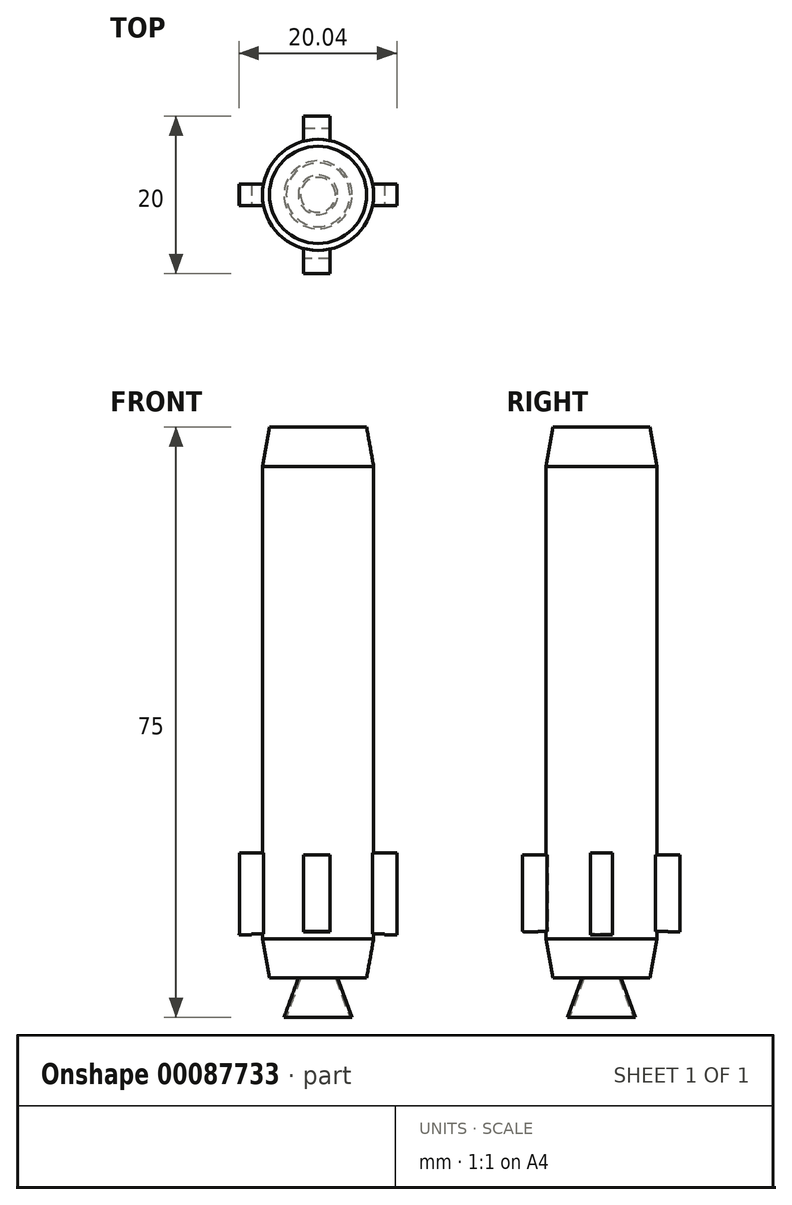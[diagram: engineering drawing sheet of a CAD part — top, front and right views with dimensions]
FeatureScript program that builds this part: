
annotation { "Feature Type Name" : "Feature", "Feature Type Description" : "" }
export const myFeature = defineFeature(function(context is Context, id is Id, definition is map)
    precondition{}
    {
        {
            var Q0;
            Q0=qCreatedBy(makeId("Top.planeOp"),FACE);
            var sketch = newSketch(context, id + "F0", { "sketchPlane" : qUnion([Q0])});
            skCircle(sketch, "E0", {"center": v(0, 0) * mm, "radius": 7.06 * mm});
            skSolve(sketch);
        }
        {
            var Q0;
            Q0 = qSketchRegion(id + "F0", true);
            extrude(context, id + "F1", {"entities" : qUnion([Q0]), "depth" : 10 * mm, "hasSecondDirection" : true, "secondDirectionOppositeDirection" : true, "secondDirectionDepth" : 50 * mm});
        }
        {
            var Q0;
            Q0=makeQuery(id+"F1.opExtrude","CAP_FACE",FACE,{"disambiguationData":[OSD([sQuery(id+"F0.wireOp",EDGE,"E0")])],"isStart":false});
            extrude(context, id + "F2", {"entities" : qUnion([Q0]), "operationType" : NewBodyOperationType.ADD, "depth" : 5 * mm, "hasDraft" : true, "draftAngle" : 10 * degree, "draftPullDirection" : true});
        }
        {
            var Q0;
            Q0=makeQuery(id+"F1.opExtrude","CAP_FACE",FACE,{"disambiguationData":[OSD([sQuery(id+"F0.wireOp",EDGE,"E0")])],"isStart":true});
            extrude(context, id + "F3", {"entities" : qUnion([Q0]), "operationType" : NewBodyOperationType.ADD, "depth" : 5 * mm, "hasDraft" : true, "draftAngle" : 10 * degree, "draftPullDirection" : true});
        }
        {
            var Q0;
            Q0=makeQuery(id+"F3.opExtrude","CAP_FACE",FACE,{"disambiguationData":[OSD([sQuery(id+"F0.wireOp",EDGE,"E0")])],"isStart":false});
            var sketch = newSketch(context, id + "F4", { "sketchPlane" : qUnion([Q0])});
            skCircle(sketch, "E1", {"center": v(0, 0) * mm, "radius": 2.5 * mm});
            skSolve(sketch);
        }
        {
            var Q0;
            Q0 = qSketchRegion(id + "F4", true);
            extrude(context, id + "F5", {"entities" : qUnion([Q0]), "operationType" : NewBodyOperationType.ADD, "depth" : 5 * mm, "hasDraft" : true, "draftAngle" : 20 * degree});
        }
        {
            var Q0;
            Q0=makeQuery(id+"F5.opExtrude","CAP_FACE",FACE,{"disambiguationData":[OSD([sQuery(id+"F4.wireOp",EDGE,"E1")])],"isStart":false});
            var sketch = newSketch(context, id + "F6", { "sketchPlane" : qUnion([Q0])});
            skCircle(sketch, "E2", {"center": v(0, 0) * mm, "radius": 4.04 * mm});
            skSolve(sketch);
        }
        {
            var Q0;
            Q0 = qSketchRegion(id + "F6", true);
            extrude(context, id + "F7", {"entities" : qUnion([Q0]), "operationType" : NewBodyOperationType.REMOVE, "oppositeDirection" : true, "depth" : 5 * mm, "hasDraft" : true, "draftAngle" : 20 * degree, "draftPullDirection" : true});
        }
        {
            var Q0;
            Q0=qCreatedBy(makeId("Right.planeOp"),FACE);
            var sketch = newSketch(context, id + "F8", { "sketchPlane" : qUnion([Q0])});
            skLineSegment(sketch, "E3.bottom", {"start": v(-1.38, -49.39) * mm, "end": v(1.38, -49.39) * mm});
            skLineSegment(sketch, "E3.top", {"start": v(-1.38, -39.07) * mm, "end": v(1.38, -39.07) * mm});
            skLineSegment(sketch, "E3.left", {"start": v(-1.38, -49.39) * mm, "end": v(-1.38, -39.07) * mm});
            skLineSegment(sketch, "E3.right", {"start": v(1.38, -49.39) * mm, "end": v(1.38, -39.07) * mm});
            skSolve(sketch);
        }
        {
            var Q0;
            Q0 = qSketchRegion(id + "F8", true);
            extrude(context, id + "F9", {"entities" : qUnion([Q0]), "operationType" : NewBodyOperationType.ADD, "depth" : 10 * mm, "hasSecondDirection" : true, "secondDirectionOppositeDirection" : true, "secondDirectionDepth" : 10 * mm});
        }
        {
            var Q0;
            {var subQ0=sQuery(id+"F8.wireOp",EDGE,"E3.left");var subQ1=sQuery(id+"F8.wireOp",EDGE,"E3.right");var subQ2=sQuery(id+"F8.wireOp",EDGE,"E3.bottom");Q0=makeQuery(id+"F9.boolean.opBoolean","SPLIT",FACE,{"disambiguationData":[TD([makeQuery(id+"F9.opExtrude","CAP_FACE",FACE,{"disambiguationData":[OSD([subQ2,sQuery(id+"F8.wireOp",EDGE,"E3.top"),subQ0,subQ1])],"isStart":false})])],"derivedFrom":makeQuery(id+"F9.opExtrude","SWEPT_FACE",FACE,{"disambiguationData":[OSD([subQ2])]})});}
            var sketch = newSketch(context, id + "F10", { "sketchPlane" : qUnion([Q0])});
            skLineSegment(sketch, "E4.bottom", {"start": v(10, -1.38) * mm, "end": v(8.46, -1.38) * mm});
            skLineSegment(sketch, "E4.top", {"start": v(10, 1.38) * mm, "end": v(8.46, 1.38) * mm});
            skLineSegment(sketch, "E4.left", {"start": v(10, -1.38) * mm, "end": v(10, 1.38) * mm});
            skLineSegment(sketch, "E4.right", {"start": v(8.46, -1.38) * mm, "end": v(8.46, 1.38) * mm});
            skLineSegment(sketch, "E5.bottom", {"start": v(-10.04, -1.38) * mm, "end": v(-8.44, -1.38) * mm});
            skLineSegment(sketch, "E5.top", {"start": v(-10.04, 1.38) * mm, "end": v(-8.44, 1.38) * mm});
            skLineSegment(sketch, "E5.left", {"start": v(-10.04, -1.38) * mm, "end": v(-10.04, 1.38) * mm});
            skLineSegment(sketch, "E5.right", {"start": v(-8.44, -1.38) * mm, "end": v(-8.44, 1.38) * mm});
            skSolve(sketch);
        }
        {
            var Q0;
            Q0 = qSketchRegion(id + "F10", true);
            extrude(context, id + "F11", {"entities" : qUnion([Q0]), "operationType" : NewBodyOperationType.ADD, "depth" : 0.1 * mm});
        }
        {
            var Q0;
            Q0=qCreatedBy(makeId("Front.planeOp"),FACE);
            var sketch = newSketch(context, id + "F12", { "sketchPlane" : qUnion([Q0])});
            skLineSegment(sketch, "E6.bottom", {"start": v(1.53, -39.38) * mm, "end": v(-1.86, -39.38) * mm});
            skLineSegment(sketch, "E6.top", {"start": v(1.53, -49.07) * mm, "end": v(-1.86, -49.07) * mm});
            skLineSegment(sketch, "E6.left", {"start": v(1.53, -39.38) * mm, "end": v(1.53, -49.07) * mm});
            skLineSegment(sketch, "E6.right", {"start": v(-1.86, -39.38) * mm, "end": v(-1.86, -49.07) * mm});
            skSolve(sketch);
        }
        {
            var Q0;
            Q0 = qSketchRegion(id + "F12", true);
            extrude(context, id + "F13", {"entities" : qUnion([Q0]), "operationType" : NewBodyOperationType.ADD, "depth" : 10 * mm, "hasSecondDirection" : true, "secondDirectionOppositeDirection" : true, "secondDirectionDepth" : 10 * mm});
        }
        {
            var Q0;
            {var subQ0=sQuery(id+"F12.wireOp",EDGE,"E6.right");var subQ1=sQuery(id+"F12.wireOp",EDGE,"E6.left");var subQ2=sQuery(id+"F12.wireOp",EDGE,"E6.top");Q0=makeQuery(id+"F13.boolean.opBoolean","SPLIT",FACE,{"disambiguationData":[TD([makeQuery(id+"F13.opExtrude","CAP_FACE",FACE,{"disambiguationData":[OSD([sQuery(id+"F12.wireOp",EDGE,"E6.bottom"),subQ2,subQ1,subQ0])],"isStart":true})])],"derivedFrom":makeQuery(id+"F13.opExtrude","SWEPT_FACE",FACE,{"disambiguationData":[OSD([subQ2])]})});}
            var sketch = newSketch(context, id + "F14", { "sketchPlane" : qUnion([Q0])});
            skLineSegment(sketch, "E7.bottom", {"start": v(-1.86, -10) * mm, "end": v(1.53, -10) * mm});
            skLineSegment(sketch, "E7.top", {"start": v(-1.86, -8.44) * mm, "end": v(1.53, -8.44) * mm});
            skLineSegment(sketch, "E7.left", {"start": v(-1.86, -10) * mm, "end": v(-1.86, -8.44) * mm});
            skLineSegment(sketch, "E7.right", {"start": v(1.53, -10) * mm, "end": v(1.53, -8.44) * mm});
            skPoint(sketch, "E8.firstSnap0", {"position": v(1.53, -9.22) * mm});
            skLineSegment(sketch, "E8.bottom", {"start": v(1.53, 9.92) * mm, "end": v(-1.86, 9.92) * mm});
            skLineSegment(sketch, "E8.top", {"start": v(1.53, 8.08) * mm, "end": v(-1.86, 8.08) * mm});
            skLineSegment(sketch, "E8.left", {"start": v(1.53, 9.92) * mm, "end": v(1.53, 8.08) * mm});
            skLineSegment(sketch, "E8.right", {"start": v(-1.86, 9.92) * mm, "end": v(-1.86, 8.08) * mm});
            skSolve(sketch);
        }
        {
            var Q0;
            Q0 = qSketchRegion(id + "F14", true);
            extrude(context, id + "F15", {"entities" : qUnion([Q0]), "operationType" : NewBodyOperationType.ADD, "depth" : 0.1 * mm});
        }
    });
